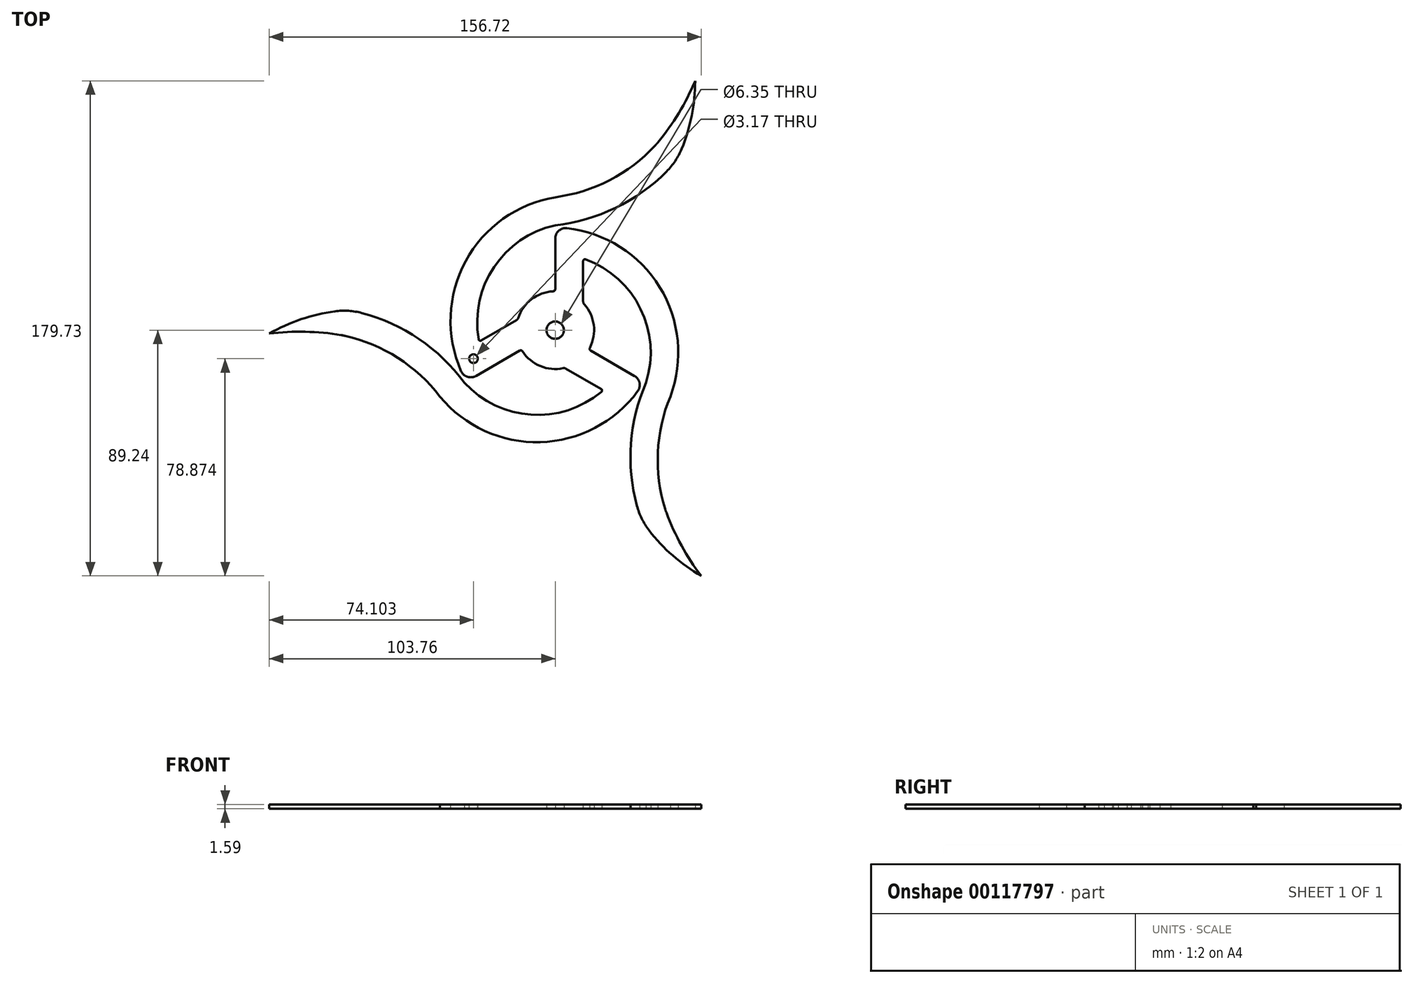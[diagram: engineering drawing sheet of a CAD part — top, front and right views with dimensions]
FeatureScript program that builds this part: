
annotation { "Feature Type Name" : "Feature", "Feature Type Description" : "" }
export const myFeature = defineFeature(function(context is Context, id is Id, definition is map)
    precondition{}
    {
        {
            var Q0;
            Q0=qCreatedBy(makeId("Top.planeOp"),FACE);
            var sketch = newSketch(context, id + "F0", { "sketchPlane" : qUnion([Q0])});
            skCircle(sketch, "E0", {"center": v(0, 0) * mm, "radius": 90.49 * mm, "construction": true});
            skLineSegment(sketch, "E1", {"start": v(0, 0) * mm, "end": v(0, 90.49) * mm, "construction": true});
            skLineSegment(sketch, "E2", {"start": v(0, 90.49) * mm, "end": v(50.8, 90.49) * mm, "construction": true});
            skCircle(sketch, "E3", {"center": v(0, 0) * mm, "radius": 38.1 * mm, "construction": true});
            skCircle(sketch, "E4.0", {"center": v(0, 0) * mm, "radius": 48.26 * mm, "construction": true});
            skLineSegment(sketch, "E5", {"start": v(50.8, 90.49) * mm, "end": v(50.8, 67.63) * mm, "construction": true});
            skLineSegment(sketch, "E6", {"start": v(50.8, 67.63) * mm, "end": v(36.83, 67.63) * mm, "construction": true});
            skCircle(sketch, "E7.0", {"center": v(0, 0) * mm, "radius": 27.94 * mm, "construction": true});
            skLineSegment(sketch, "E8", {"start": v(43.82, 67.63) * mm, "end": v(43.82, 61.28) * mm, "construction": true});
            skArc(sketch, "E9", {"start": v(0, 48.26) * mm, "mid": v(19.8, 54.48) * mm, "end": v(36.31, 67.06) * mm});
            skArc(sketch, "E10", {"start": v(37.27, 68.15) * mm, "mid": v(44.84, 78.83) * mm, "end": v(50.8, 90.49) * mm});
            skArc(sketch, "E11", {"start": v(0, 38.1) * mm, "mid": v(21.9, 44.41) * mm, "end": v(40.45, 57.64) * mm});
            skArc(sketch, "E12", {"start": v(45.91, 65.85) * mm, "mid": v(49.57, 77.93) * mm, "end": v(50.8, 90.49) * mm});
            skPoint(sketch, "E13.visualSharp", {"position": v(43.82, 61.28) * mm});
            skArc(sketch, "E13.filletArc", {"start": v(40.45, 57.64) * mm, "mid": v(43.59, 61.47) * mm, "end": v(45.91, 65.85) * mm});
            skPoint(sketch, "E14.visualSharp", {"position": v(36.83, 67.63) * mm});
            skArc(sketch, "E14.filletArc", {"start": v(36.31, 67.06) * mm, "mid": v(36.8, 67.6) * mm, "end": v(37.27, 68.15) * mm});
            skPoint(sketch, "E15.1.0", {"position": v(-74.98, 7.3) * mm});
            skArc(sketch, "E15.1.1", {"start": v(-77.66, -1.8) * mm, "mid": v(-90.7, -0.58) * mm, "end": v(-103.76, -1.25) * mm});
            skLineSegment(sketch, "E15.1.2", {"start": v(-103.76, -1.25) * mm, "end": v(-83.97, 10.18) * mm, "construction": true});
            skPoint(sketch, "E15.1.3", {"position": v(-76.98, -1.92) * mm});
            skArc(sketch, "E15.1.4", {"start": v(-41.8, -24.13) * mm, "mid": v(-57.08, -10.1) * mm, "end": v(-76.24, -2.08) * mm});
            skLineSegment(sketch, "E15.1.5", {"start": v(-78.36, -45.24) * mm, "end": v(-103.76, -1.25) * mm, "construction": true});
            skArc(sketch, "E15.1.6", {"start": v(-79.98, 6.84) * mm, "mid": v(-92.27, 3.96) * mm, "end": v(-103.76, -1.25) * mm});
            skArc(sketch, "E15.1.7", {"start": v(-33, -19.05) * mm, "mid": v(-49.4, -3.24) * mm, "end": v(-70.14, 6.21) * mm});
            skLineSegment(sketch, "E15.1.8", {"start": v(-83.97, 10.18) * mm, "end": v(-76.98, -1.92) * mm, "construction": true});
            skLineSegment(sketch, "E15.1.9", {"start": v(-80.47, 4.13) * mm, "end": v(-74.98, 7.3) * mm, "construction": true});
            skArc(sketch, "E15.1.10", {"start": v(-70.14, 6.21) * mm, "mid": v(-75.03, 7) * mm, "end": v(-79.98, 6.84) * mm});
            skArc(sketch, "E15.1.11", {"start": v(-76.24, -2.08) * mm, "mid": v(-76.94, -1.93) * mm, "end": v(-77.66, -1.8) * mm});
            skLineSegment(sketch, "E15.1.12", {"start": v(0, 0) * mm, "end": v(-78.36, -45.24) * mm, "construction": true});
            skPoint(sketch, "E15.2.0", {"position": v(31.16, -68.58) * mm});
            skArc(sketch, "E15.2.1", {"start": v(40.39, -66.35) * mm, "mid": v(45.85, -78.25) * mm, "end": v(52.96, -89.24) * mm});
            skLineSegment(sketch, "E15.2.2", {"start": v(52.96, -89.24) * mm, "end": v(33.17, -77.8) * mm, "construction": true});
            skPoint(sketch, "E15.2.3", {"position": v(40.15, -65.7) * mm});
            skArc(sketch, "E15.2.4", {"start": v(41.8, -24.13) * mm, "mid": v(37.28, -44.4) * mm, "end": v(39.92, -64.98) * mm});
            skLineSegment(sketch, "E15.2.5", {"start": v(78.36, -45.24) * mm, "end": v(52.96, -89.24) * mm, "construction": true});
            skArc(sketch, "E15.2.6", {"start": v(34.07, -72.69) * mm, "mid": v(42.7, -81.89) * mm, "end": v(52.96, -89.24) * mm});
            skArc(sketch, "E15.2.7", {"start": v(33, -19.05) * mm, "mid": v(27.51, -41.17) * mm, "end": v(29.69, -63.85) * mm});
            skLineSegment(sketch, "E15.2.8", {"start": v(33.17, -77.8) * mm, "end": v(40.15, -65.7) * mm, "construction": true});
            skLineSegment(sketch, "E15.2.9", {"start": v(36.66, -71.76) * mm, "end": v(31.16, -68.58) * mm, "construction": true});
            skArc(sketch, "E15.2.10", {"start": v(29.69, -63.85) * mm, "mid": v(31.45, -68.48) * mm, "end": v(34.07, -72.69) * mm});
            skArc(sketch, "E15.2.11", {"start": v(39.92, -64.98) * mm, "mid": v(40.15, -65.67) * mm, "end": v(40.39, -66.35) * mm});
            skLineSegment(sketch, "E15.2.12", {"start": v(0, 0) * mm, "end": v(78.36, -45.24) * mm, "construction": true});
            skCircle(sketch, "E16", {"center": v(0, 0) * mm, "radius": 3.18 * mm});
            skArc(sketch, "E17", {"start": v(-13.44, 4.35) * mm, "mid": v(-13.51, 4.12) * mm, "end": v(-13.58, 3.89) * mm});
            skLineSegment(sketch, "E18", {"start": v(0, 27.94) * mm, "end": v(0, 14.13) * mm});
            skCircle(sketch, "E19.0", {"center": v(0, 0) * mm, "radius": 20.32 * mm, "construction": true});
            skLineSegment(sketch, "E20.0", {"start": v(10.16, 25.13) * mm, "end": v(10.16, 10.32) * mm});
            skArc(sketch, "E21", {"start": v(33, -19.05) * mm, "mid": v(30.97, 7.74) * mm, "end": v(11.01, 25.73) * mm});
            skCircle(sketch, "E22.0", {"center": v(0, 0) * mm, "radius": 37.3 * mm, "construction": true});
            skLineSegment(sketch, "E23", {"start": v(0, 27.94) * mm, "end": v(0, 37.3) * mm});
            skArc(sketch, "E24", {"start": v(41.8, -24.13) * mm, "mid": v(36.79, 17.4) * mm, "end": v(0, 37.3) * mm});
            skPoint(sketch, "E25.visualSharp", {"position": v(10.16, 26.03) * mm});
            skArc(sketch, "E25.filletArc", {"start": v(11.01, 25.73) * mm, "mid": v(10.43, 25.65) * mm, "end": v(10.16, 25.13) * mm});
            skPoint(sketch, "E26.visualSharp", {"position": v(10.16, 9.82) * mm});
            skArc(sketch, "E26.filletArc", {"start": v(10.16, 10.32) * mm, "mid": v(10.24, 9.86) * mm, "end": v(10.49, 9.47) * mm});
            skArc(sketch, "E27.1.0", {"start": v(0, 48.26) * mm, "mid": v(-33.46, 23.16) * mm, "end": v(-32.3, -18.65) * mm});
            skArc(sketch, "E27.1.1", {"start": v(0, 38.1) * mm, "mid": v(-22.2, 22.95) * mm, "end": v(-27.79, -3.32) * mm});
            skPoint(sketch, "E27.1.2", {"position": v(-27.62, -4.21) * mm});
            skArc(sketch, "E27.1.3", {"start": v(-27.79, -3.32) * mm, "mid": v(-27.43, -3.8) * mm, "end": v(-26.84, -3.77) * mm});
            skLineSegment(sketch, "E27.1.4", {"start": v(-26.84, -3.77) * mm, "end": v(-14.02, 3.64) * mm});
            skArc(sketch, "E27.1.5", {"start": v(-12.24, -7.06) * mm, "mid": v(-5.52, -13) * mm, "end": v(3.42, -13.7) * mm});
            skLineSegment(sketch, "E27.1.6", {"start": v(-24.2, -13.97) * mm, "end": v(-32.3, -18.65) * mm});
            skLineSegment(sketch, "E27.1.7", {"start": v(-24.2, -13.97) * mm, "end": v(-12.24, -7.06) * mm});
            skArc(sketch, "E27.2.0", {"start": v(-41.8, -24.13) * mm, "mid": v(-3.33, -40.56) * mm, "end": v(32.3, -18.65) * mm});
            skArc(sketch, "E27.2.1", {"start": v(-33, -19.05) * mm, "mid": v(-8.78, -30.7) * mm, "end": v(16.77, -22.4) * mm});
            skPoint(sketch, "E27.2.2", {"position": v(17.46, -21.81) * mm});
            skArc(sketch, "E27.2.3", {"start": v(16.77, -22.4) * mm, "mid": v(17, -21.86) * mm, "end": v(16.68, -21.36) * mm});
            skLineSegment(sketch, "E27.2.4", {"start": v(16.68, -21.36) * mm, "end": v(3.86, -13.96) * mm});
            skArc(sketch, "E27.2.5", {"start": v(12.24, -7.06) * mm, "mid": v(14.05, 1.49) * mm, "end": v(10.49, 9.47) * mm});
            skLineSegment(sketch, "E27.2.6", {"start": v(24.2, -13.97) * mm, "end": v(32.3, -18.65) * mm});
            skLineSegment(sketch, "E27.2.7", {"start": v(24.2, -13.97) * mm, "end": v(12.24, -7.06) * mm});
            skPoint(sketch, "E28.1.0", {"position": v(-13.58, 3.89) * mm});
            skArc(sketch, "E28.1.1", {"start": v(-14.02, 3.64) * mm, "mid": v(-13.66, 3.94) * mm, "end": v(-13.44, 4.35) * mm});
            skPoint(sketch, "E28.2.0", {"position": v(3.42, -13.7) * mm});
            skArc(sketch, "E28.2.1", {"start": v(3.86, -13.96) * mm, "mid": v(3.42, -13.8) * mm, "end": v(2.96, -13.82) * mm});
            skArc(sketch, "E29.trimOffspring", {"start": v(-12.24, -7.06) * mm, "mid": v(-5.74, -12.91) * mm, "end": v(2.96, -13.82) * mm});
            skArc(sketch, "E30.trimOffspring", {"start": v(12.24, -7.06) * mm, "mid": v(14.02, 1.72) * mm, "end": v(10.16, 9.82) * mm});
            skArc(sketch, "E31.trimOffspring", {"start": v(0, 14.13) * mm, "mid": v(-8.5, 11.28) * mm, "end": v(-13.58, 3.89) * mm});
            skArc(sketch, "E32.trimOffspring", {"start": v(0, 14.13) * mm, "mid": v(-8.31, 11.42) * mm, "end": v(-13.44, 4.35) * mm});
            skSolve(sketch);
        }
        {
            var Q0;
            Q0=makeQuery(id+"F0.imprint","IMPRINT",FACE,{"disambiguationData":[TD([[makeQuery(id+"F0.imprint","IMPRINT",EDGE,{"derivedFrom":sQuery(id+"F0.wireOp",EDGE,"E15.2.1")}),-1.0]])]});
            var sketch = newSketch(context, id + "F1", { "sketchPlane" : qUnion([Q0])});
            skSolve(sketch);
        }
        {
            var Q0;
            Q0=makeQuery(id+"F0.imprint","IMPRINT",FACE,{"disambiguationData":[TD([[makeQuery(id+"F0.imprint","IMPRINT",EDGE,{"derivedFrom":sQuery(id+"F0.wireOp",EDGE,"E9")}),-1.0]])]});
            extrude(context, id + "F2", {"entities" : qUnion([Q0]), "depth" : 1.59 * mm});
        }
        {
            var Q0;
            Q0=makeQuery(id+"F2.opExtrude","SWEPT_EDGE",EDGE,{"disambiguationData":[OSD([sQuery(id+"F0.wireOp",EDGE,"E23"),sQuery(id+"F0.wireOp",EDGE,"E24")])]});
            var Q1;
            Q1=makeQuery(id+"F2.opExtrude","SWEPT_EDGE",EDGE,{"disambiguationData":[OSD([sQuery(id+"F0.wireOp",EDGE,"E27.1.0"),sQuery(id+"F0.wireOp",EDGE,"E27.1.6")])]});
            var Q2;
            Q2=makeQuery(id+"F2.opExtrude","SWEPT_EDGE",EDGE,{"disambiguationData":[OSD([sQuery(id+"F0.wireOp",EDGE,"E27.2.0"),sQuery(id+"F0.wireOp",EDGE,"E27.2.6")])]});
            fillet(context, id + "F3", {"entities" : qUnion([Q0, Q1, Q2]), "radius" : 3.8 * mm, "tangentPropagation" : true, "allowEdgeOverflow" : false});
        }
        {
            var Q0;
            Q0=makeQuery(id+"F2.opExtrude","SWEPT_EDGE",EDGE,{"disambiguationData":[OSD([sQuery(id+"F0.wireOp",EDGE,"E27.2.7"),sQuery(id+"F0.wireOp",EDGE,"E30.trimOffspring")])]});
            var Q1;
            Q1=makeQuery(id+"F2.opExtrude","SWEPT_EDGE",EDGE,{"disambiguationData":[OSD([sQuery(id+"F0.wireOp",EDGE,"E18"),sQuery(id+"F0.wireOp",EDGE,"E32.trimOffspring")])]});
            var Q2;
            Q2=makeQuery(id+"F2.opExtrude","SWEPT_EDGE",EDGE,{"disambiguationData":[OSD([sQuery(id+"F0.wireOp",EDGE,"E27.1.7"),sQuery(id+"F0.wireOp",EDGE,"E29.trimOffspring")])]});
            fillet(context, id + "F4", {"entities" : qUnion([Q0, Q1, Q2]), "radius" : 0.76 * mm, "tangentPropagation" : true, "allowEdgeOverflow" : false});
        }
        {
            var Q0;
            Q0=makeQuery(id+"F1.imprint","IMPRINT",FACE,{"disambiguationData":[TD([[makeQuery(id+"F1.imprint","IMPRINT",EDGE,{"derivedFrom":makeQuery(id+"F0.imprint","IMPRINT",EDGE,{"derivedFrom":sQuery(id+"F0.wireOp",EDGE,"E9")})}),-1.0]])]});
            var sketch = newSketch(context, id + "F5", { "sketchPlane" : qUnion([Q0])});
            skArc(sketch, "E33.0", {"start": v(-27.79, -3.32) * mm, "mid": v(-27.43, -3.8) * mm, "end": v(-26.84, -3.77) * mm, "construction": true});
            skArc(sketch, "E34.0", {"start": v(-28.79, -16.62) * mm, "mid": v(-31.88, -16.94) * mm, "end": v(-34.19, -14.85) * mm, "construction": true});
            skLineSegment(sketch, "E35", {"start": v(-31.88, -16.94) * mm, "end": v(-27.43, -3.8) * mm, "construction": true});
            skCircle(sketch, "E36", {"center": v(-29.66, -10.37) * mm, "radius": 1.59 * mm});
            skPoint(sketch, "E37.center", {"position": v(0, 0) * mm});
            skSolve(sketch);
        }
        {
            var Q0;
            Q0 = qSketchRegion(id + "F5", true);
            extrude(context, id + "F6", {"entities" : qUnion([Q0]), "operationType" : NewBodyOperationType.REMOVE, "endBound" : BoundingType.UP_TO_NEXT, "depth" : 25.4 * mm});
        }
    });
